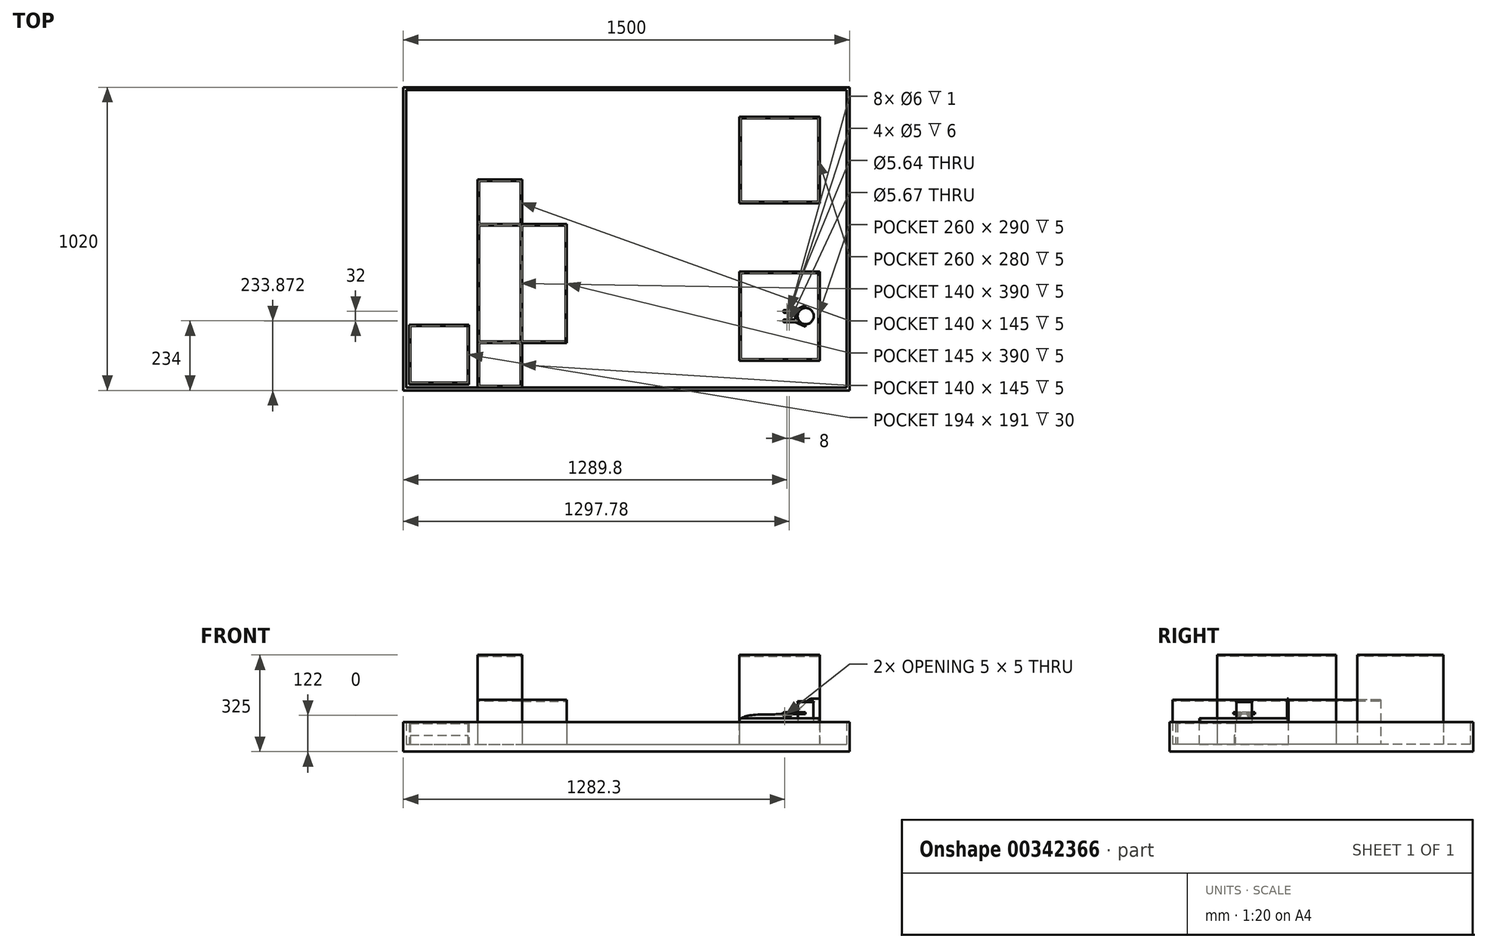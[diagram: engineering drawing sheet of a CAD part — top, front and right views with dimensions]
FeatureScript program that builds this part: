
annotation { "Feature Type Name" : "Feature", "Feature Type Description" : "" }
export const myFeature = defineFeature(function(context is Context, id is Id, definition is map)
    precondition{}
    {
        {
            var Q0;
            Q0=qCreatedBy(makeId("Top.planeOp"),FACE);
            var sketch = newSketch(context, id + "F0", { "sketchPlane" : qUnion([Q0])});
            skCircle(sketch, "E0", {"center": v(0, 0) * mm, "radius": 27.2 * mm});
            skSolve(sketch);
        }
        {
            var Q0;
            Q0=qSketchRegion(id+"F0",true);
            extrude(context, id + "F1", {"entities" : qUnion([Q0]), "depth" : 2.83 * mm});
        }
        {
            var Q0;
            Q0=makeQuery(id+"F1.opExtrude","CAP_FACE",FACE,{"disambiguationData":[OSD([sQuery(id+"F0.wireOp",EDGE,"E0")])],"isStart":false});
            var sketch = newSketch(context, id + "F2", { "sketchPlane" : qUnion([Q0])});
            skCircle(sketch, "E1", {"center": v(0, 0) * mm, "radius": 26.4 * mm});
            skSolve(sketch);
        }
        {
            var Q0;
            Q0=qSketchRegion(id+"F2",true);
            extrude(context, id + "F3", {"entities" : qUnion([Q0]), "operationType" : NewBodyOperationType.ADD, "depth" : 67.36 * mm});
        }
        {
            var Q0;
            Q0=makeQuery(id+"F3.opExtrude","CAP_FACE",FACE,{"disambiguationData":[OSD([sQuery(id+"F2.wireOp",EDGE,"E1")])],"isStart":false});
            var sketch = newSketch(context, id + "F4", { "sketchPlane" : qUnion([Q0])});
            skCircle(sketch, "E2", {"center": v(0, 0) * mm, "radius": 27.2 * mm});
            skSolve(sketch);
        }
        {
            var Q0;
            Q0=qSketchRegion(id+"F4",true);
            extrude(context, id + "F5", {"entities" : qUnion([Q0]), "operationType" : NewBodyOperationType.ADD, "depth" : 2.83 * mm});
        }
        {
            var Q0;
            Q0=makeQuery(id+"F5.opExtrude","CAP_FACE",FACE,{"disambiguationData":[OSD([sQuery(id+"F4.wireOp",EDGE,"E2")])],"isStart":false});
            var sketch = newSketch(context, id + "F6", { "sketchPlane" : qUnion([Q0])});
            skSolve(sketch);
        }
        {
            var Q0;
            Q0=qCreatedBy(makeId("Top.planeOp"),FACE);
            cPlane(context, id + "F7", {"entities" : qUnion([Q0]), "cplaneType" : CPlaneType.OFFSET, "offset" : 25 * mm, "width" : 150 * mm, "height" : 150 * mm});
        }
        {
            var Q0;
            Q0=makeQuery(id+"F6.imprint","IMPRINT",FACE,{"disambiguationData":[TD([[makeQuery(id+"F6.imprint","IMPRINT",EDGE,{"derivedFrom":makeQuery(id+"F5.opExtrude","CAP_EDGE",EDGE,{"disambiguationData":[OSD([sQuery(id+"F4.wireOp",EDGE,"E2")])],"isStart":false})}),1.0]])]});
            var sketch = newSketch(context, id + "F8", { "sketchPlane" : qUnion([Q0])});
            skSolve(sketch);
        }
        {
            var Q0;
            Q0=qCreatedBy(makeId("Top.planeOp"),FACE);
            var sketch = newSketch(context, id + "F9", { "sketchPlane" : qUnion([Q0])});
            skLineSegment(sketch, "E3.bottom", {"start": v(-222.8, -150) * mm, "end": v(47.2, -150) * mm});
            skLineSegment(sketch, "E3.top", {"start": v(-222.8, 150) * mm, "end": v(47.2, 150) * mm});
            skLineSegment(sketch, "E3.left", {"start": v(-222.8, -150) * mm, "end": v(-222.8, 150) * mm});
            skLineSegment(sketch, "E3.right", {"start": v(47.2, -150) * mm, "end": v(47.2, 150) * mm});
            skSolve(sketch);
        }
        {
            var Q0;
            Q0=qSketchRegion(id+"F9",true);
            extrude(context, id + "F10", {"entities" : qUnion([Q0]), "oppositeDirection" : true, "depth" : 72 * mm});
        }
        {
            var Q0;
            Q0=makeQuery(id+"F10.opExtrude","CAP_FACE",FACE,{"disambiguationData":[OSD([sQuery(id+"F9.wireOp",EDGE,"E3.bottom"),sQuery(id+"F9.wireOp",EDGE,"E3.top"),sQuery(id+"F9.wireOp",EDGE,"E3.left"),sQuery(id+"F9.wireOp",EDGE,"E3.right")])],"isStart":true});
            var sketch = newSketch(context, id + "F11", { "sketchPlane" : qUnion([Q0])});
            skLineSegment(sketch, "E4.bottom", {"start": v(-222.8, -150) * mm, "end": v(47.2, -150) * mm});
            skLineSegment(sketch, "E4.top", {"start": v(-222.8, -145) * mm, "end": v(42.2, -145) * mm});
            skLineSegment(sketch, "E4.left", {"start": v(-222.8, -150) * mm, "end": v(-222.8, -145) * mm});
            skLineSegment(sketch, "E5.bottom", {"start": v(47.2, 150) * mm, "end": v(42.2, 150) * mm});
            skLineSegment(sketch, "E5.left", {"start": v(47.2, 150) * mm, "end": v(47.2, -150) * mm});
            skLineSegment(sketch, "E5.right", {"start": v(42.2, 150) * mm, "end": v(42.2, -145) * mm});
            skSolve(sketch);
        }
        {
            var Q0;
            Q0=qSketchRegion(id+"F11",true);
            extrude(context, id + "F12", {"entities" : qUnion([Q0]), "operationType" : NewBodyOperationType.ADD, "depth" : 15 * mm});
        }
        {
            var Q0;
            Q0=makeQuery(id+"F12.boolean.opBoolean","MERGE",FACE,{"derivedFrom":[makeQuery(id+"F10.opExtrude","SWEPT_FACE",FACE,{"disambiguationData":[OSD([sQuery(id+"F9.wireOp",EDGE,"E3.top")])]}),makeQuery(id+"F12.opExtrude","SWEPT_FACE",FACE,{"disambiguationData":[OSD([sQuery(id+"F11.wireOp",EDGE,"E5.bottom")])]})]});
            var sketch = newSketch(context, id + "F13", { "sketchPlane" : qUnion([Q0])});
            skLineSegment(sketch, "E6", {"start": v(-47.2, 81.36) * mm, "end": v(-21.31, 81.36) * mm});
            skFitSpline(sketch, "E7", {"points": [v(-21.31, 81.36) * mm, v(15.24, 52.01) * mm, v(114.14, 28.17) * mm, v(222.8, 0) * mm], "startDerivative": vector(181.02, 0.3) * mm, "endDerivative": vector(-1.73, -239.85) * mm});
            skLineSegment(sketch, "E8", {"start": v(-47.2, 81.36) * mm, "end": v(-47.2, -72) * mm});
            skLineSegment(sketch, "E9", {"start": v(-47.2, -72) * mm, "end": v(222.8, -72) * mm});
            skLineSegment(sketch, "E10", {"start": v(222.8, -72) * mm, "end": v(222.8, 0) * mm});
            skSolve(sketch);
        }
        {
            var Q0;
            Q0=qSketchRegion(id+"F13",true);
            extrude(context, id + "F14", {"entities" : qUnion([Q0]), "operationType" : NewBodyOperationType.ADD, "oppositeDirection" : true, "depth" : 5 * mm});
        }
        {
            var Q0;
            Q0=makeQuery(id+"F10.opExtrude","CAP_FACE",FACE,{"disambiguationData":[OSD([sQuery(id+"F9.wireOp",EDGE,"E3.bottom"),sQuery(id+"F9.wireOp",EDGE,"E3.top"),sQuery(id+"F9.wireOp",EDGE,"E3.left"),sQuery(id+"F9.wireOp",EDGE,"E3.right")])],"isStart":true});
            var sketch = newSketch(context, id + "F15", { "sketchPlane" : qUnion([Q0])});
            skLineSegment(sketch, "E11.bottom", {"start": v(-222.8, 145) * mm, "end": v(-217.8, 145) * mm});
            skLineSegment(sketch, "E11.top", {"start": v(-222.8, -145) * mm, "end": v(-217.8, -145) * mm});
            skLineSegment(sketch, "E11.left", {"start": v(-222.8, 145) * mm, "end": v(-222.8, -145) * mm});
            skLineSegment(sketch, "E11.right", {"start": v(-217.8, 145) * mm, "end": v(-217.8, -145) * mm});
            skSolve(sketch);
        }
        {
            var Q0;
            Q0=qSketchRegion(id+"F15",true);
            extrude(context, id + "F16", {"entities" : qUnion([Q0]), "operationType" : NewBodyOperationType.ADD, "depth" : 5 * mm});
        }
        {
            var Q0;
            Q0=makeQuery(id+"F10.opExtrude","CAP_FACE",FACE,{"disambiguationData":[OSD([sQuery(id+"F9.wireOp",EDGE,"E3.bottom"),sQuery(id+"F9.wireOp",EDGE,"E3.top"),sQuery(id+"F9.wireOp",EDGE,"E3.left"),sQuery(id+"F9.wireOp",EDGE,"E3.right")])],"isStart":false});
            var sketch = newSketch(context, id + "F17", { "sketchPlane" : qUnion([Q0])});
            skLineSegment(sketch, "E12.bottom", {"start": v(147.2, 250) * mm, "end": v(-1352.8, 250) * mm});
            skLineSegment(sketch, "E12.top", {"start": v(147.2, -770) * mm, "end": v(-1352.8, -770) * mm});
            skLineSegment(sketch, "E12.left", {"start": v(147.2, 250) * mm, "end": v(147.2, -770) * mm});
            skLineSegment(sketch, "E12.right", {"start": v(-1352.8, 250) * mm, "end": v(-1352.8, -770) * mm});
            skSolve(sketch);
        }
        {
            var Q0;
            Q0=qSketchRegion(id+"F17",true);
            extrude(context, id + "F18", {"entities" : qUnion([Q0]), "operationType" : NewBodyOperationType.ADD, "depth" : 25 * mm});
        }
        {
            var Q0;
            Q0=makeQuery(id+"F18.opExtrude","CAP_FACE",FACE,{"disambiguationData":[OSD([sQuery(id+"F17.wireOp",EDGE,"E12.bottom"),sQuery(id+"F17.wireOp",EDGE,"E12.top"),sQuery(id+"F17.wireOp",EDGE,"E12.left"),sQuery(id+"F17.wireOp",EDGE,"E12.right")])],"isStart":true});
            var sketch = newSketch(context, id + "F19", { "sketchPlane" : qUnion([Q0])});
            skLineSegment(sketch, "E13.bottom", {"start": v(-222.8, 670) * mm, "end": v(47.2, 670) * mm});
            skLineSegment(sketch, "E13.top", {"start": v(-222.8, 380) * mm, "end": v(47.2, 380) * mm});
            skLineSegment(sketch, "E13.left", {"start": v(-222.8, 670) * mm, "end": v(-222.8, 380) * mm});
            skLineSegment(sketch, "E13.right", {"start": v(47.2, 670) * mm, "end": v(47.2, 380) * mm});
            skSolve(sketch);
        }
        {
            var Q0;
            Q0=qSketchRegion(id+"F19",true);
            extrude(context, id + "F20", {"entities" : qUnion([Q0]), "operationType" : NewBodyOperationType.ADD, "depth" : 300 * mm});
        }
        {
            var Q0;
            Q0=makeQuery(id+"F20.opExtrude","CAP_FACE",FACE,{"disambiguationData":[OSD([sQuery(id+"F19.wireOp",EDGE,"E13.bottom"),sQuery(id+"F19.wireOp",EDGE,"E13.top"),sQuery(id+"F19.wireOp",EDGE,"E13.left"),sQuery(id+"F19.wireOp",EDGE,"E13.right")])],"isStart":false});
            var sketch = newSketch(context, id + "F21", { "sketchPlane" : qUnion([Q0])});
            skLineSegment(sketch, "E14.bottom", {"start": v(-217.8, 665) * mm, "end": v(42.2, 665) * mm});
            skLineSegment(sketch, "E14.top", {"start": v(-217.8, 385) * mm, "end": v(42.2, 385) * mm});
            skLineSegment(sketch, "E14.left", {"start": v(-217.8, 665) * mm, "end": v(-217.8, 385) * mm});
            skLineSegment(sketch, "E14.right", {"start": v(42.2, 665) * mm, "end": v(42.2, 385) * mm});
            skSolve(sketch);
        }
        {
            var Q0;
            Q0=qSketchRegion(id+"F21",true);
            extrude(context, id + "F22", {"entities" : qUnion([Q0]), "operationType" : NewBodyOperationType.REMOVE, "oppositeDirection" : true, "depth" : 5 * mm});
        }
        {
            var Q0;
            Q0=makeQuery(id+"F18.opExtrude","CAP_FACE",FACE,{"disambiguationData":[OSD([sQuery(id+"F17.wireOp",EDGE,"E12.bottom"),sQuery(id+"F17.wireOp",EDGE,"E12.top"),sQuery(id+"F17.wireOp",EDGE,"E12.left"),sQuery(id+"F17.wireOp",EDGE,"E12.right")])],"isStart":true});
            var sketch = newSketch(context, id + "F23", { "sketchPlane" : qUnion([Q0])});
            skLineSegment(sketch, "E15.bottom", {"start": v(-1352.8, 770) * mm, "end": v(147.2, 770) * mm});
            skLineSegment(sketch, "E15.top", {"start": v(-1352.8, -250) * mm, "end": v(147.2, -250) * mm});
            skLineSegment(sketch, "E15.left", {"start": v(-1352.8, 770) * mm, "end": v(-1352.8, -250) * mm});
            skLineSegment(sketch, "E15.right", {"start": v(147.2, 770) * mm, "end": v(147.2, -250) * mm});
            skLineSegment(sketch, "E16.bottom", {"start": v(-1342.8, 760) * mm, "end": v(137.2, 760) * mm});
            skLineSegment(sketch, "E16.top", {"start": v(-1342.8, -240) * mm, "end": v(137.2, -240) * mm});
            skLineSegment(sketch, "E16.left", {"start": v(-1342.8, 760) * mm, "end": v(-1342.8, -240) * mm});
            skLineSegment(sketch, "E16.right", {"start": v(137.2, 760) * mm, "end": v(137.2, -240) * mm});
            skSolve(sketch);
        }
        {
            var Q0;
            Q0=qSketchRegion(id+"F23",true);
            extrude(context, id + "F24", {"entities" : qUnion([Q0]), "operationType" : NewBodyOperationType.ADD, "depth" : 75 * mm});
        }
        {
            var Q0;
            Q0=makeQuery(id+"F18.opExtrude","CAP_FACE",FACE,{"disambiguationData":[OSD([sQuery(id+"F17.wireOp",EDGE,"E12.bottom"),sQuery(id+"F17.wireOp",EDGE,"E12.top"),sQuery(id+"F17.wireOp",EDGE,"E12.left"),sQuery(id+"F17.wireOp",EDGE,"E12.right")])],"isStart":true});
            var sketch = newSketch(context, id + "F25", { "sketchPlane" : qUnion([Q0])});
            skLineSegment(sketch, "E17.bottom", {"start": v(-1102.8, 460) * mm, "end": v(-952.8, 460) * mm});
            skLineSegment(sketch, "E17.top", {"start": v(-1102.8, -240) * mm, "end": v(-952.8, -240) * mm});
            skLineSegment(sketch, "E17.left", {"start": v(-1102.8, 460) * mm, "end": v(-1102.8, -240) * mm});
            skLineSegment(sketch, "E17.right", {"start": v(-952.8, 460) * mm, "end": v(-952.8, 310) * mm});
            skLineSegment(sketch, "E18.bottom", {"start": v(-952.8, 310) * mm, "end": v(-802.8, 310) * mm});
            skLineSegment(sketch, "E18.top", {"start": v(-952.8, -90) * mm, "end": v(-802.8, -90) * mm});
            skLineSegment(sketch, "E18.right", {"start": v(-802.8, 310) * mm, "end": v(-802.8, -90) * mm});
            skLineSegment(sketch, "E19.trimOffspring", {"start": v(-952.8, -90) * mm, "end": v(-952.8, -240) * mm});
            skSolve(sketch);
        }
        {
            var Q0;
            Q0=qSketchRegion(id+"F25",true);
            extrude(context, id + "F26", {"entities" : qUnion([Q0]), "operationType" : NewBodyOperationType.ADD, "depth" : 150 * mm});
        }
        {
            var Q0;
            Q0=makeQuery(id+"F26.opExtrude","CAP_FACE",FACE,{"disambiguationData":[OSD([sQuery(id+"F25.wireOp",EDGE,"E17.bottom"),sQuery(id+"F25.wireOp",EDGE,"E17.top"),sQuery(id+"F25.wireOp",EDGE,"E17.left"),sQuery(id+"F25.wireOp",EDGE,"E17.right"),sQuery(id+"F25.wireOp",EDGE,"E18.bottom"),sQuery(id+"F25.wireOp",EDGE,"E18.top"),sQuery(id+"F25.wireOp",EDGE,"E18.right"),sQuery(id+"F25.wireOp",EDGE,"E19.trimOffspring")])],"isStart":false});
            var sketch = newSketch(context, id + "F27", { "sketchPlane" : qUnion([Q0])});
            skLineSegment(sketch, "E20.bottom", {"start": v(-952.8, 310) * mm, "end": v(-1102.8, 310) * mm});
            skLineSegment(sketch, "E20.top", {"start": v(-952.8, -90) * mm, "end": v(-1102.8, -90) * mm});
            skLineSegment(sketch, "E20.left", {"start": v(-952.8, 310) * mm, "end": v(-952.8, -90) * mm});
            skLineSegment(sketch, "E20.right", {"start": v(-1102.8, 310) * mm, "end": v(-1102.8, -90) * mm});
            skSolve(sketch);
        }
        {
            var Q0;
            Q0=qSketchRegion(id+"F27",true);
            extrude(context, id + "F28", {"entities" : qUnion([Q0]), "operationType" : NewBodyOperationType.ADD, "depth" : 150 * mm});
        }
        {
            var Q0;
            Q0=makeQuery(id+"F28.opExtrude","CAP_FACE",FACE,{"disambiguationData":[OSD([sQuery(id+"F27.wireOp",EDGE,"E20.bottom"),sQuery(id+"F27.wireOp",EDGE,"E20.top"),sQuery(id+"F27.wireOp",EDGE,"E20.left"),sQuery(id+"F27.wireOp",EDGE,"E20.right")])],"isStart":false});
            var sketch = newSketch(context, id + "F29", { "sketchPlane" : qUnion([Q0])});
            skLineSegment(sketch, "E21.bottom", {"start": v(-1097.8, 305) * mm, "end": v(-957.8, 305) * mm});
            skLineSegment(sketch, "E21.top", {"start": v(-1097.8, -85) * mm, "end": v(-957.8, -85) * mm});
            skLineSegment(sketch, "E21.left", {"start": v(-1097.8, 305) * mm, "end": v(-1097.8, -85) * mm});
            skLineSegment(sketch, "E21.right", {"start": v(-957.8, 305) * mm, "end": v(-957.8, -85) * mm});
            skSolve(sketch);
        }
        {
            var Q0;
            Q0=qSketchRegion(id+"F29",true);
            extrude(context, id + "F30", {"entities" : qUnion([Q0]), "operationType" : NewBodyOperationType.REMOVE, "oppositeDirection" : true, "depth" : 5 * mm});
        }
        {
            var Q0;
            {var subQ0=sQuery(id+"F25.wireOp",EDGE,"E17.left");var subQ1=sQuery(id+"F25.wireOp",EDGE,"E18.bottom");var subQ2=sQuery(id+"F25.wireOp",EDGE,"E17.right");var subQ3=sQuery(id+"F25.wireOp",EDGE,"E17.bottom");var subQ4=makeQuery(id+"F26.opExtrude","CAP_FACE",FACE,{"disambiguationData":[OSD([subQ3,sQuery(id+"F25.wireOp",EDGE,"E17.top"),subQ0,subQ2,subQ1,sQuery(id+"F25.wireOp",EDGE,"E18.top"),sQuery(id+"F25.wireOp",EDGE,"E18.right"),sQuery(id+"F25.wireOp",EDGE,"E19.trimOffspring")])],"isStart":false});Q0=makeQuery(id+"F28.boolean.opBoolean","SPLIT",FACE,{"disambiguationData":[TD([makeQuery(id+"F26.opExtrude","SWEPT_FACE",FACE,{"disambiguationData":[OSD([subQ3])]})])],"derivedFrom":subQ4});}
            var sketch = newSketch(context, id + "F31", { "sketchPlane" : qUnion([Q0])});
            skLineSegment(sketch, "E22.bottom", {"start": v(-1097.8, 455) * mm, "end": v(-957.8, 455) * mm});
            skLineSegment(sketch, "E22.top", {"start": v(-1097.8, 310) * mm, "end": v(-957.8, 310) * mm});
            skLineSegment(sketch, "E22.left", {"start": v(-1097.8, 455) * mm, "end": v(-1097.8, 310) * mm});
            skLineSegment(sketch, "E22.right", {"start": v(-957.8, 455) * mm, "end": v(-957.8, 310) * mm});
            skLineSegment(sketch, "E23.bottom", {"start": v(-952.8, 305) * mm, "end": v(-807.8, 305) * mm});
            skLineSegment(sketch, "E23.top", {"start": v(-952.8, -85) * mm, "end": v(-807.8, -85) * mm});
            skLineSegment(sketch, "E23.left", {"start": v(-952.8, 305) * mm, "end": v(-952.8, -85) * mm});
            skLineSegment(sketch, "E23.right", {"start": v(-807.8, 305) * mm, "end": v(-807.8, -85) * mm});
            skLineSegment(sketch, "E24.bottom", {"start": v(-1097.8, -90) * mm, "end": v(-957.8, -90) * mm});
            skLineSegment(sketch, "E24.top", {"start": v(-1097.8, -235) * mm, "end": v(-957.8, -235) * mm});
            skLineSegment(sketch, "E24.left", {"start": v(-1097.8, -90) * mm, "end": v(-1097.8, -235) * mm});
            skLineSegment(sketch, "E24.right", {"start": v(-957.8, -90) * mm, "end": v(-957.8, -235) * mm});
            skSolve(sketch);
        }
        {
            var Q0;
            Q0=qSketchRegion(id+"F31",true);
            extrude(context, id + "F32", {"entities" : qUnion([Q0]), "operationType" : NewBodyOperationType.REMOVE, "oppositeDirection" : true, "depth" : 5 * mm});
        }
        {
            var Q0;
            Q0=qCreatedBy(id+"F7.planeOp",FACE);
            var sketch = newSketch(context, id + "F33", { "sketchPlane" : qUnion([Q0])});
            skLineSegment(sketch, "E25", {"start": v(0, 0) * mm, "end": v(-90, 0) * mm, "construction": true});
            skLineSegment(sketch, "E26.bottom", {"start": v(-74.5, -12) * mm, "end": v(-55, -12) * mm});
            skLineSegment(sketch, "E26.top", {"start": v(-74.5, -20) * mm, "end": v(-55, -20) * mm});
            skLineSegment(sketch, "E26.left", {"start": v(-74.5, -12) * mm, "end": v(-74.5, -13) * mm});
            skPoint(sketch, "E27.visualSharp", {"position": v(-51, -12) * mm});
            skPoint(sketch, "E28.visualSharp", {"position": v(-51, -20) * mm});
            skCircle(sketch, "E29", {"center": v(-55, -16) * mm, "radius": 3 * mm});
            skLineSegment(sketch, "E30", {"start": v(-59, -3.98) * mm, "end": v(-59, -18.08) * mm, "construction": true});
            skCircle(sketch, "E31.MirrorC", {"center": v(-63, -16) * mm, "radius": 3 * mm});
            skLineSegment(sketch, "E32.bottom", {"start": v(-74.5, -13) * mm, "end": v(-65.65, -13) * mm});
            skLineSegment(sketch, "E32.top", {"start": v(-74.5, -19) * mm, "end": v(-65.65, -19) * mm});
            skArc(sketch, "E33", {"start": v(-65.65, -13) * mm, "mid": v(-67, -16) * mm, "end": v(-65.65, -19) * mm});
            skLineSegment(sketch, "E34.trimOffspring", {"start": v(-74.5, -19) * mm, "end": v(-74.5, -20) * mm});
            skArc(sketch, "E35.trimOffspring", {"start": v(-55, -20) * mm, "mid": v(-51, -16) * mm, "end": v(-55, -12) * mm});
            skLineSegment(sketch, "E36.MirrorCS", {"start": v(-74.5, 12) * mm, "end": v(-74.5, 13) * mm});
            skLineSegment(sketch, "E37.MirrorCS", {"start": v(-74.5, 19) * mm, "end": v(-74.5, 20) * mm});
            skPoint(sketch, "E38.MirrorP", {"position": v(-51, 12) * mm});
            skLineSegment(sketch, "E39.MirrorCS", {"start": v(-74.5, 12) * mm, "end": v(-55, 12) * mm});
            skPoint(sketch, "E40.MirrorP", {"position": v(-51, 20) * mm});
            skArc(sketch, "E41.MirrorCS", {"start": v(-65.65, 13) * mm, "mid": v(-67, 16) * mm, "end": v(-65.65, 19) * mm});
            skArc(sketch, "E42.MirrorCS", {"start": v(-55, 20) * mm, "mid": v(-51, 16) * mm, "end": v(-55, 12) * mm});
            skLineSegment(sketch, "E43.MirrorCS", {"start": v(-74.5, 20) * mm, "end": v(-55, 20) * mm});
            skCircle(sketch, "E44.MirrorC", {"center": v(-55, 16) * mm, "radius": 3 * mm});
            skCircle(sketch, "E45.MirrorC", {"center": v(-63, 16) * mm, "radius": 3 * mm});
            skLineSegment(sketch, "E46.MirrorCS", {"start": v(-74.5, 19) * mm, "end": v(-65.65, 19) * mm});
            skLineSegment(sketch, "E47.MirrorCS", {"start": v(-74.5, 13) * mm, "end": v(-65.65, 13) * mm});
            skSolve(sketch);
        }
        {
            var Q0;
            Q0=qSketchRegion(id+"F33",true);
            var Q1;
            Q1=qSketchRegion(id+"F36",true);
            extrude(context, id + "F34", {"entities" : qUnion([Q0, Q1]), "endBound" : BoundingType.SYMMETRIC, "depth" : 8 * mm});
        }
        {
            var Q0;
            Q0=makeQuery(id+"F34.opExtrude","CAP_EDGE",EDGE,{"disambiguationData":[OSD([sQuery(id+"F33.wireOp",EDGE,"E34.trimOffspring")])],"isStart":false});
            var Q1;
            Q1=makeQuery(id+"F34.opExtrude","CAP_EDGE",EDGE,{"disambiguationData":[OSD([sQuery(id+"F33.wireOp",EDGE,"E26.left")])],"isStart":false});
            var Q2;
            Q2=makeQuery(id+"F34.opExtrude","CAP_EDGE",EDGE,{"disambiguationData":[OSD([sQuery(id+"F33.wireOp",EDGE,"E34.trimOffspring")])],"isStart":true});
            var Q3;
            Q3=makeQuery(id+"F34.opExtrude","CAP_EDGE",EDGE,{"disambiguationData":[OSD([sQuery(id+"F33.wireOp",EDGE,"E26.left")])],"isStart":true});
            var Q4;
            Q4=makeQuery(id+"F34.opExtrude","CAP_EDGE",EDGE,{"disambiguationData":[OSD([sQuery(id+"F33.wireOp",EDGE,"E36.MirrorCS")])],"isStart":false});
            var Q5;
            Q5=makeQuery(id+"F34.opExtrude","CAP_EDGE",EDGE,{"disambiguationData":[OSD([sQuery(id+"F33.wireOp",EDGE,"E37.MirrorCS")])],"isStart":false});
            var Q6;
            Q6=makeQuery(id+"F34.opExtrude","CAP_EDGE",EDGE,{"disambiguationData":[OSD([sQuery(id+"F33.wireOp",EDGE,"E37.MirrorCS")])],"isStart":true});
            var Q7;
            Q7=makeQuery(id+"F34.opExtrude","CAP_EDGE",EDGE,{"disambiguationData":[OSD([sQuery(id+"F33.wireOp",EDGE,"E36.MirrorCS")])],"isStart":true});
            fillet(context, id + "F35", {"entities" : qUnion([Q0, Q1, Q2, Q3, Q4, Q5, Q6, Q7]), "radius" : 4 * mm, "tangentPropagation" : true, "allowEdgeOverflow" : false});
        }
        {
            var Q0;
            Q0=makeQuery(id+"F34.opExtrude","SWEPT_FACE",FACE,{"disambiguationData":[OSD([sQuery(id+"F33.wireOp",EDGE,"E26.top")])]});
            var sketch = newSketch(context, id + "F36", { "sketchPlane" : qUnion([Q0])});
            skCircle(sketch, "E48", {"center": v(-70.5, 25) * mm, "radius": 3 * mm});
            skSolve(sketch);
        }
        {
            var Q0;
            Q0=qSketchRegion(id+"F36",true);
            var Q1;
            Q1=makeQuery(id+"F34.opExtrude","SWEPT_FACE",FACE,{"disambiguationData":[OSD([sQuery(id+"F33.wireOp",EDGE,"E26.bottom")])]});
            extrude(context, id + "F37", {"entities" : qUnion([Q0]), "operationType" : NewBodyOperationType.ADD, "endBound" : BoundingType.UP_TO_SURFACE, "oppositeDirection" : true, "endBoundEntityFace" : qUnion([Q1]), "depth" : 25 * mm});
        }
        {
            var Q0;
            Q0=makeQuery(id+"F34.opExtrude","SWEPT_FACE",FACE,{"disambiguationData":[OSD([sQuery(id+"F33.wireOp",EDGE,"E43.MirrorCS")])]});
            var sketch = newSketch(context, id + "F38", { "sketchPlane" : qUnion([Q0])});
            skCircle(sketch, "E49", {"center": v(70.5, 25) * mm, "radius": 3 * mm});
            skSolve(sketch);
        }
        {
            var Q0;
            Q0=qSketchRegion(id+"F38",true);
            var Q1;
            Q1=makeQuery(id+"F34.opExtrude","SWEPT_FACE",FACE,{"disambiguationData":[OSD([sQuery(id+"F33.wireOp",EDGE,"E39.MirrorCS")])]});
            extrude(context, id + "F39", {"entities" : qUnion([Q0]), "operationType" : NewBodyOperationType.ADD, "endBound" : BoundingType.UP_TO_SURFACE, "oppositeDirection" : true, "endBoundEntityFace" : qUnion([Q1]), "depth" : 25 * mm});
        }
        {
            var Q0;
            Q0=qCreatedBy(id+"F7.planeOp",FACE);
            var sketch = newSketch(context, id + "F40", { "sketchPlane" : qUnion([Q0])});
            skCircle(sketch, "E50", {"center": v(-55, 16) * mm, "radius": 3 * mm});
            skCircle(sketch, "E51", {"center": v(-63, 16) * mm, "radius": 2.5 * mm});
            skCircle(sketch, "E52", {"center": v(-63, 16) * mm, "radius": 3 * mm});
            skCircle(sketch, "E53", {"center": v(-55, 16) * mm, "radius": 2.5 * mm});
            skSolve(sketch);
        }
        {
            var Q0;
            Q0=qSketchRegion(id+"F40",true);
            extrude(context, id + "F41", {"entities" : qUnion([Q0]), "operationType" : NewBodyOperationType.ADD, "endBound" : BoundingType.SYMMETRIC, "depth" : 6 * mm});
        }
        {
            var Q0;
            Q0=qCreatedBy(id+"F7.planeOp",FACE);
            var sketch = newSketch(context, id + "F42", { "sketchPlane" : qUnion([Q0])});
            skCircle(sketch, "E54", {"center": v(-63, -16) * mm, "radius": 2.5 * mm});
            skCircle(sketch, "E55", {"center": v(-63, -16) * mm, "radius": 3 * mm});
            skCircle(sketch, "E56", {"center": v(-55, -16) * mm, "radius": 2.5 * mm});
            skCircle(sketch, "E57", {"center": v(-55, -16) * mm, "radius": 3 * mm});
            skSolve(sketch);
        }
        {
            var Q0;
            Q0=qSketchRegion(id+"F42",true);
            extrude(context, id + "F43", {"entities" : qUnion([Q0]), "operationType" : NewBodyOperationType.ADD, "endBound" : BoundingType.SYMMETRIC, "depth" : 6 * mm});
        }
        {
            var Q0;
            Q0=makeQuery(id+"F34.opExtrude","SWEPT_FACE",FACE,{"disambiguationData":[OSD([sQuery(id+"F33.wireOp",EDGE,"E43.MirrorCS")])]});
            var sketch = newSketch(context, id + "F44", { "sketchPlane" : qUnion([Q0])});
            skArc(sketch, "E58", {"start": v(71.5, 27.3) * mm, "mid": v(70.5, 27.5) * mm, "end": v(69.5, 27.3) * mm});
            skLineSegment(sketch, "E59.bottom", {"start": v(68.2, 26) * mm, "end": v(69.5, 26) * mm});
            skLineSegment(sketch, "E59.top", {"start": v(68.2, 24) * mm, "end": v(69.5, 24) * mm});
            skLineSegment(sketch, "E60.left", {"start": v(71.5, 27.3) * mm, "end": v(71.5, 26) * mm});
            skLineSegment(sketch, "E60.right", {"start": v(69.5, 27.3) * mm, "end": v(69.5, 26) * mm});
            skPoint(sketch, "E61.orphan", {"position": v(69.5, 27.8) * mm});
            skPoint(sketch, "E62.orphan", {"position": v(71.5, 27.8) * mm});
            skArc(sketch, "E63.trimOffspring", {"start": v(68.2, 26) * mm, "mid": v(68, 25) * mm, "end": v(68.2, 24) * mm});
            skPoint(sketch, "E59.left.start.orphan", {"position": v(67.32, 26) * mm});
            skPoint(sketch, "E64.orphan", {"position": v(67.32, 24) * mm});
            skArc(sketch, "E65.trimOffspring", {"start": v(69.5, 22.7) * mm, "mid": v(70.5, 22.5) * mm, "end": v(71.5, 22.7) * mm});
            skLineSegment(sketch, "E66.trimOffspring", {"start": v(69.5, 24) * mm, "end": v(69.5, 22.7) * mm});
            skLineSegment(sketch, "E67.trimOffspring", {"start": v(71.5, 26) * mm, "end": v(72.8, 26) * mm});
            skLineSegment(sketch, "E68.trimOffspring", {"start": v(71.5, 24) * mm, "end": v(71.5, 22.7) * mm});
            skLineSegment(sketch, "E69.trimOffspring", {"start": v(71.5, 24) * mm, "end": v(72.8, 24) * mm});
            skPoint(sketch, "E60.top.end.orphan", {"position": v(69.5, 22.2) * mm});
            skPoint(sketch, "E70.orphan", {"position": v(71.5, 22.2) * mm});
            skPoint(sketch, "E59.right.end.orphan", {"position": v(73.68, 24) * mm});
            skPoint(sketch, "E71.orphan", {"position": v(73.68, 26) * mm});
            skArc(sketch, "E72.trimOffspring", {"start": v(72.8, 24) * mm, "mid": v(73, 25) * mm, "end": v(72.8, 26) * mm});
            skSolve(sketch);
        }
        {
            var Q0;
            Q0=qSketchRegion(id+"F44",true);
            extrude(context, id + "F45", {"entities" : qUnion([Q0]), "operationType" : NewBodyOperationType.REMOVE, "endBound" : BoundingType.THROUGH_ALL, "oppositeDirection" : true, "depth" : 25 * mm});
        }
        {
            var Q0;
            Q0=makeQuery(id+"F18.opExtrude","CAP_FACE",FACE,{"disambiguationData":[OSD([sQuery(id+"F17.wireOp",EDGE,"E12.bottom"),sQuery(id+"F17.wireOp",EDGE,"E12.top"),sQuery(id+"F17.wireOp",EDGE,"E12.left"),sQuery(id+"F17.wireOp",EDGE,"E12.right")])],"isStart":true});
            var sketch = newSketch(context, id + "F46", { "sketchPlane" : qUnion([Q0])});
            skLineSegment(sketch, "E73.bottom", {"start": v(-1332.8, -30) * mm, "end": v(-1132.8, -30) * mm});
            skLineSegment(sketch, "E73.top", {"start": v(-1332.8, -230) * mm, "end": v(-1132.8, -230) * mm});
            skLineSegment(sketch, "E73.left", {"start": v(-1332.8, -30) * mm, "end": v(-1332.8, -230) * mm});
            skLineSegment(sketch, "E73.right", {"start": v(-1132.8, -30) * mm, "end": v(-1132.8, -230) * mm});
            skLineSegment(sketch, "E74.bottom", {"start": v(-1329.8, -33) * mm, "end": v(-1135.8, -33) * mm});
            skLineSegment(sketch, "E74.top", {"start": v(-1329.8, -224) * mm, "end": v(-1135.8, -224) * mm});
            skLineSegment(sketch, "E74.left", {"start": v(-1329.8, -33) * mm, "end": v(-1329.8, -224) * mm});
            skLineSegment(sketch, "E74.right", {"start": v(-1135.8, -33) * mm, "end": v(-1135.8, -224) * mm});
            skSolve(sketch);
        }
        {
            var Q0;
            Q0=qSketchRegion(id+"F46",true);
            extrude(context, id + "F47", {"entities" : qUnion([Q0]), "operationType" : NewBodyOperationType.ADD, "depth" : 30 * mm});
        }
        {
            var Q0;
            Q0=makeQuery(id+"F47.opExtrude","CAP_FACE",FACE,{"disambiguationData":[OSD([sQuery(id+"F46.wireOp",EDGE,"E73.bottom"),sQuery(id+"F46.wireOp",EDGE,"E73.top"),sQuery(id+"F46.wireOp",EDGE,"E73.left"),sQuery(id+"F46.wireOp",EDGE,"E73.right"),sQuery(id+"F46.wireOp",EDGE,"E74.bottom"),sQuery(id+"F46.wireOp",EDGE,"E74.top"),sQuery(id+"F46.wireOp",EDGE,"E74.left"),sQuery(id+"F46.wireOp",EDGE,"E74.right")])],"isStart":false});
            var sketch = newSketch(context, id + "F48", { "sketchPlane" : qUnion([Q0])});
            skLineSegment(sketch, "E75.bottom", {"start": v(-1332.8, -30) * mm, "end": v(-1329.8, -30) * mm});
            skLineSegment(sketch, "E75.top", {"start": v(-1332.8, -230) * mm, "end": v(-1329.8, -230) * mm});
            skLineSegment(sketch, "E75.left", {"start": v(-1332.8, -30) * mm, "end": v(-1332.8, -230) * mm});
            skLineSegment(sketch, "E75.right", {"start": v(-1329.8, -30) * mm, "end": v(-1329.8, -224) * mm});
            skLineSegment(sketch, "E76.bottom", {"start": v(-1329.8, -230) * mm, "end": v(-1135.8, -230) * mm});
            skLineSegment(sketch, "E76.top", {"start": v(-1329.8, -224) * mm, "end": v(-1135.8, -224) * mm});
            skLineSegment(sketch, "E77.bottom", {"start": v(-1135.8, -230) * mm, "end": v(-1132.8, -230) * mm});
            skLineSegment(sketch, "E77.top", {"start": v(-1135.8, -30) * mm, "end": v(-1132.8, -30) * mm});
            skLineSegment(sketch, "E77.left", {"start": v(-1135.8, -224) * mm, "end": v(-1135.8, -30) * mm});
            skLineSegment(sketch, "E77.right", {"start": v(-1132.8, -230) * mm, "end": v(-1132.8, -30) * mm});
            skSolve(sketch);
        }
        {
            var Q0;
            Q0=qSketchRegion(id+"F48",true);
            extrude(context, id + "F49", {"entities" : qUnion([Q0]), "operationType" : NewBodyOperationType.ADD, "depth" : 40 * mm});
        }
        {
            var Q0;
            Q0=makeQuery(id+"F34.opExtrude","CAP_FACE",FACE,{"disambiguationData":[OSD([sQuery(id+"F33.wireOp",EDGE,"E36.MirrorCS"),sQuery(id+"F33.wireOp",EDGE,"E37.MirrorCS"),sQuery(id+"F33.wireOp",EDGE,"E39.MirrorCS"),sQuery(id+"F33.wireOp",EDGE,"E41.MirrorCS"),sQuery(id+"F33.wireOp",EDGE,"E42.MirrorCS"),sQuery(id+"F33.wireOp",EDGE,"E43.MirrorCS"),sQuery(id+"F33.wireOp",EDGE,"E44.MirrorC"),sQuery(id+"F33.wireOp",EDGE,"E45.MirrorC"),sQuery(id+"F33.wireOp",EDGE,"E46.MirrorCS"),sQuery(id+"F33.wireOp",EDGE,"E47.MirrorCS")])],"isStart":false});
            var sketch = newSketch(context, id + "F50", { "sketchPlane" : qUnion([Q0])});
            skLineSegment(sketch, "E78", {"start": v(-70.88, 20) * mm, "end": v(-35.52, 20) * mm});
            skLineSegment(sketch, "E79", {"start": v(-74.88, 16) * mm, "end": v(-74.88, 15.31) * mm});
            skLineSegment(sketch, "E80", {"start": v(-70.88, 11.31) * mm, "end": v(-39.52, 11.31) * mm});
            skLineSegment(sketch, "E81", {"start": v(-35.52, 7.31) * mm, "end": v(-35.52, -7.14) * mm});
            skLineSegment(sketch, "E82", {"start": v(-39.52, -11.14) * mm, "end": v(-70.88, -11.14) * mm});
            skLineSegment(sketch, "E83", {"start": v(-74.88, -15.14) * mm, "end": v(-74.88, -16.57) * mm});
            skLineSegment(sketch, "E84", {"start": v(-70.88, -20.57) * mm, "end": v(-35.52, -20.57) * mm});
            skLineSegment(sketch, "E85", {"start": v(-35.52, -20.57) * mm, "end": v(-0.6, -36.37) * mm});
            skLineSegment(sketch, "E86", {"start": v(-35.52, 20) * mm, "end": v(-1.7, 37.1) * mm});
            skLineSegment(sketch, "E87", {"start": v(-1.7, 37.1) * mm, "end": v(-1.7, 29.33) * mm});
            skLineSegment(sketch, "E88", {"start": v(-0.6, -36.37) * mm, "end": v(-0.6, -30) * mm});
            skArc(sketch, "E89", {"start": v(-1.7, 29.33) * mm, "mid": v(-29.44, -0.86) * mm, "end": v(-0.6, -30) * mm});
            skCircle(sketch, "E90", {"center": v(-63, 16) * mm, "radius": 2.82 * mm});
            skCircle(sketch, "E91", {"center": v(-55, 16) * mm, "radius": 2.71 * mm});
            skCircle(sketch, "E92", {"center": v(-63, -16) * mm, "radius": 2.6 * mm});
            skCircle(sketch, "E93", {"center": v(-55.02, -16.13) * mm, "radius": 2.83 * mm});
            skArc(sketch, "E94.filletArc", {"start": v(-35.52, 7.31) * mm, "mid": v(-36.7, 10.14) * mm, "end": v(-39.52, 11.31) * mm});
            skArc(sketch, "E95.filletArc", {"start": v(-39.52, -11.14) * mm, "mid": v(-36.7, -9.97) * mm, "end": v(-35.52, -7.14) * mm});
            skArc(sketch, "E96.filletArc", {"start": v(-74.88, 15.31) * mm, "mid": v(-73.71, 12.48) * mm, "end": v(-70.88, 11.31) * mm});
            skArc(sketch, "E97.filletArc", {"start": v(-70.88, 20) * mm, "mid": v(-73.71, 18.83) * mm, "end": v(-74.88, 16) * mm});
            skArc(sketch, "E98.filletArc", {"start": v(-70.88, -11.14) * mm, "mid": v(-73.71, -12.31) * mm, "end": v(-74.88, -15.14) * mm});
            skArc(sketch, "E99.filletArc", {"start": v(-74.88, -16.57) * mm, "mid": v(-73.71, -19.4) * mm, "end": v(-70.88, -20.57) * mm});
            skSolve(sketch);
        }
        {
            var Q0;
            Q0 = qSketchRegion(id + "F50", true);
            extrude(context, id + "F51", {"entities" : qUnion([Q0]), "depth" : 6 * mm});
        }
    });
